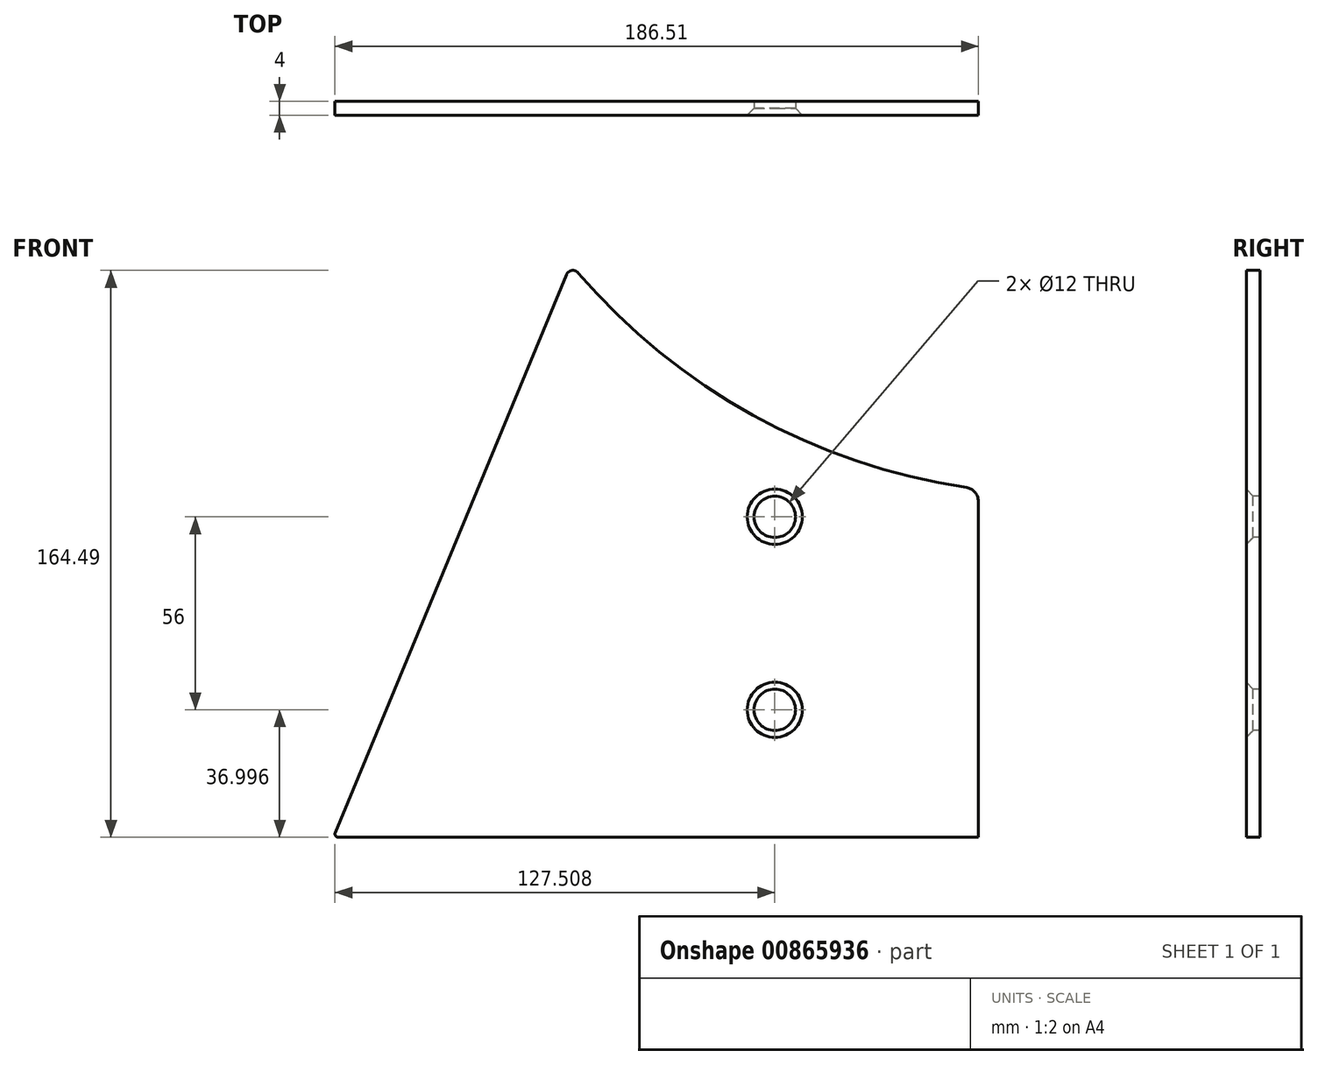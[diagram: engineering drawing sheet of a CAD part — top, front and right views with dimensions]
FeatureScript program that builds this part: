
annotation { "Feature Type Name" : "Feature", "Feature Type Description" : "" }
export const myFeature = defineFeature(function(context is Context, id is Id, definition is map)
    precondition{}
    {
        {
            var Q0;
            Q0=qCreatedBy(makeId("Front.planeOp"),FACE);
            var sketch = newSketch(context, id + "F0", { "sketchPlane" : qUnion([Q0])});
            skLineSegment(sketch, "E0", {"start": v(77.86, -44.11) * mm, "end": v(-107.65, -44.11) * mm});
            skLineSegment(sketch, "E1", {"start": v(-41.52, 119.14) * mm, "end": v(-108.57, -42.73) * mm});
            skLineSegment(sketch, "E2", {"start": v(77.86, -44.11) * mm, "end": v(77.86, 53.4) * mm});
            skArc(sketch, "E3", {"start": v(-38.15, 119.68) * mm, "mid": v(12.52, 78.36) * mm, "end": v(74.45, 57.36) * mm});
            skPoint(sketch, "E3.third.point", {"position": v(9.3, 80.19) * mm});
            skPoint(sketch, "E4.visualSharp", {"position": v(-40.26, 122.18) * mm});
            skArc(sketch, "E4.filletArc", {"start": v(-38.15, 119.68) * mm, "mid": v(-39.99, 120.35) * mm, "end": v(-41.52, 119.14) * mm});
            skPoint(sketch, "E5.visualSharp", {"position": v(-109.14, -44.11) * mm});
            skArc(sketch, "E5.filletArc", {"start": v(-108.57, -42.73) * mm, "mid": v(-108.48, -43.67) * mm, "end": v(-107.65, -44.11) * mm});
            skPoint(sketch, "E6.visualSharp", {"position": v(77.86, 56.89) * mm});
            skArc(sketch, "E6.filletArc", {"start": v(77.86, 53.4) * mm, "mid": v(76.89, 56.02) * mm, "end": v(74.45, 57.36) * mm});
            skSolve(sketch);
        }
        {
            var Q0;
            Q0 = qSketchRegion(id + "F0", true);
            extrude(context, id + "F1", {"entities" : qUnion([Q0]), "depth" : 4 * mm, "offsetDistance" : 25 * mm});
        }
        {
            var Q0;
            Q0=makeQuery(id+"F1.opExtrude","CAP_FACE",FACE,{"disambiguationData":[OSD([sQuery(id+"F0.wireOp",EDGE,"E0"),sQuery(id+"F0.wireOp",EDGE,"E1"),sQuery(id+"F0.wireOp",EDGE,"E2"),sQuery(id+"F0.wireOp",EDGE,"E3"),sQuery(id+"F0.wireOp",EDGE,"E4.filletArc"),sQuery(id+"F0.wireOp",EDGE,"E5.filletArc"),sQuery(id+"F0.wireOp",EDGE,"E6.filletArc")])],"isStart":false});
            var sketch = newSketch(context, id + "F2", { "sketchPlane" : qUnion([Q0])});
            skPoint(sketch, "E7", {"position": v(18.86, 48.89) * mm});
            skPoint(sketch, "E8", {"position": v(18.86, -7.11) * mm});
            skSolve(sketch);
        }
        {
            var Q0;
            Q0=sQuery(id+"F2.wireOp",VERTEX,"E7");
            var Q1;
            Q1=sQuery(id+"F2.wireOp",VERTEX,"E8");
            var Q2;
            Q2=makeQuery(id+"F1.opExtrude","SWEPT_BODY",BODY,{"disambiguationData":[OSD([sQuery(id+"F0.wireOp",EDGE,"E0"),sQuery(id+"F0.wireOp",EDGE,"E1"),sQuery(id+"F0.wireOp",EDGE,"E2"),sQuery(id+"F0.wireOp",EDGE,"E3"),sQuery(id+"F0.wireOp",EDGE,"E4.filletArc"),sQuery(id+"F0.wireOp",EDGE,"E5.filletArc"),sQuery(id+"F0.wireOp",EDGE,"E6.filletArc")])]});
            hole(context, id + "F3", {"style" : HoleStyle.C_SINK, "endStyle" : HoleEndStyle.THROUGH, "standardTappedOrClearance" : lookupTablePath({ "standard" : "ISO", "size" : "12", "type" : "Drilled" }), "standardBlindInLast" : lookupTablePath({ "standard" : "ISO", "size" : "12", "type" : "Drilled" }), "holeDiameter" : 12 * mm, "cSinkDiameter" : 16 * mm, "cSinkAngle" : 90 * degree, "majorDiameter" : 10 * mm, "isTappedThrough" : true, "tappedDepth" : 27.9 * mm, "tapClearance" : 3, "startFromSketch" : true, "locations" : qUnion([Q0, Q1]), "scope" : qUnion([Q2])});
        }
    });
